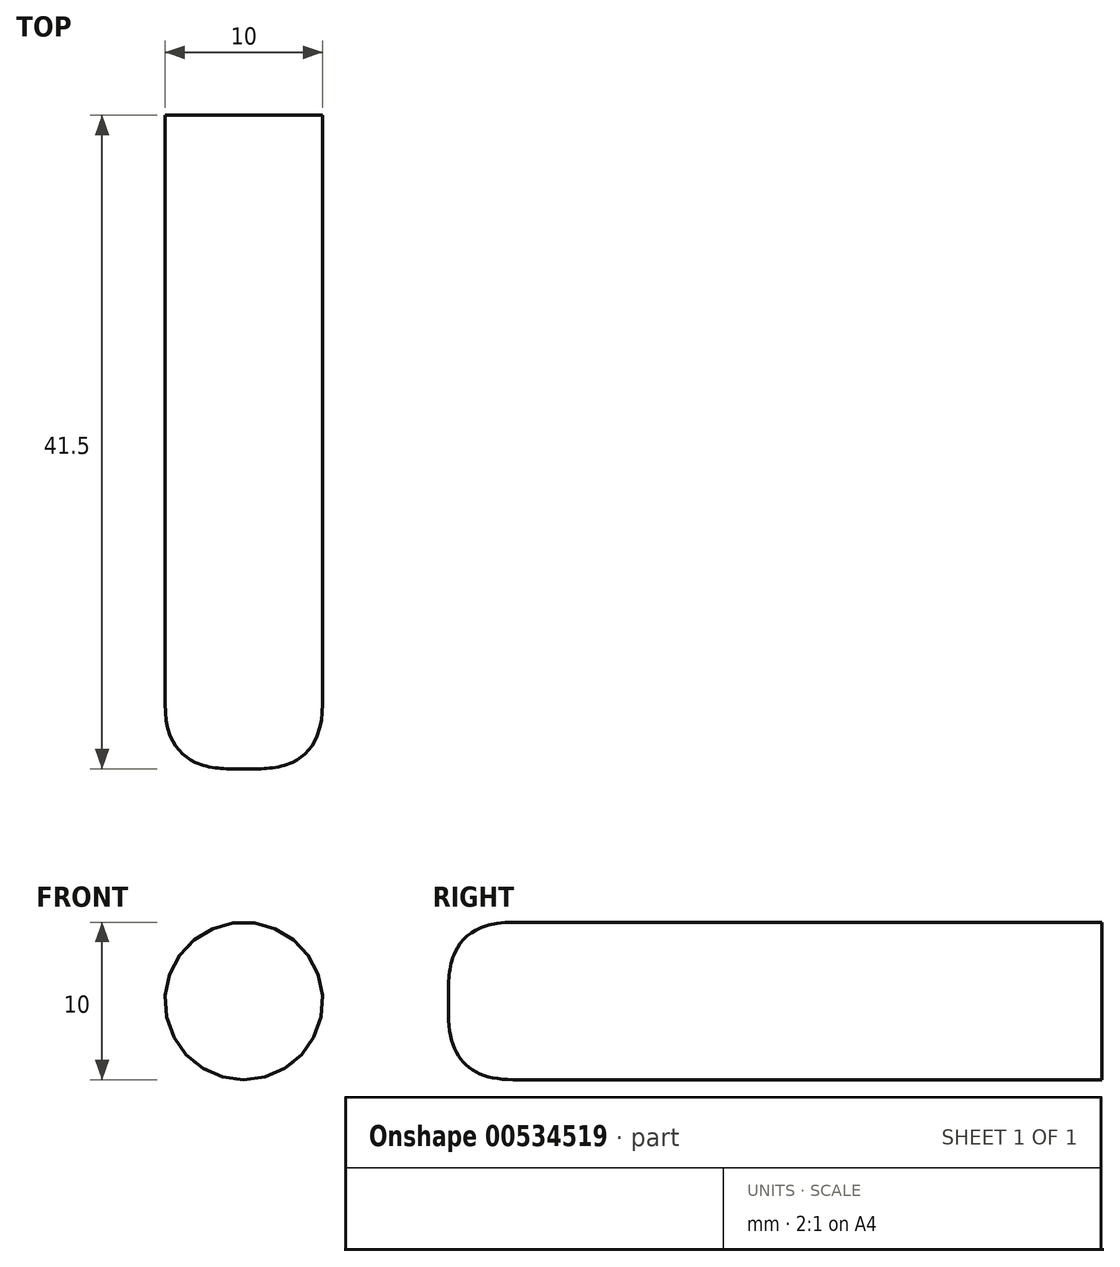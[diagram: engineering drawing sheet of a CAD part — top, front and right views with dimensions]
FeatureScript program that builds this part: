
annotation { "Feature Type Name" : "Feature", "Feature Type Description" : "" }
export const myFeature = defineFeature(function(context is Context, id is Id, definition is map)
    precondition{}
    {
        {
            var Q0;
            Q0=qCreatedBy(makeId("Front.planeOp"),FACE);
            var sketch = newSketch(context, id + "F0", { "sketchPlane" : qUnion([Q0])});
            skCircle(sketch, "E0", {"center": v(0, 0) * mm, "radius": 5 * mm});
            skSolve(sketch);
        }
        {
            var Q0;
            Q0=makeQuery(id+"F0.imprint","IMPRINT",FACE,{"disambiguationData":[TD([[makeQuery(id+"F0.imprint","IMPRINT",EDGE,{"derivedFrom":sQuery(id+"F0.wireOp",EDGE,"E0")}),1.0]])]});
            extrude(context, id + "F1", {"entities" : qUnion([Q0]), "endBound" : BoundingType.SYMMETRIC, "oppositeDirection" : true, "depth" : 41.5 * mm});
        }
        {
            var Q0;
            Q0=makeQuery(id+"F1.opExtrude","CAP_EDGE",EDGE,{"disambiguationData":[OSD([sQuery(id+"F0.wireOp",EDGE,"E0")])],"isStart":true});
            fillet(context, id + "F2", {"entities" : qUnion([Q0]), "radius" : 4.1 * mm, "tangentPropagation" : true, "rho" : 0.5, "crossSection" : FilletCrossSection.CONIC, "allowEdgeOverflow" : false});
        }
    });
